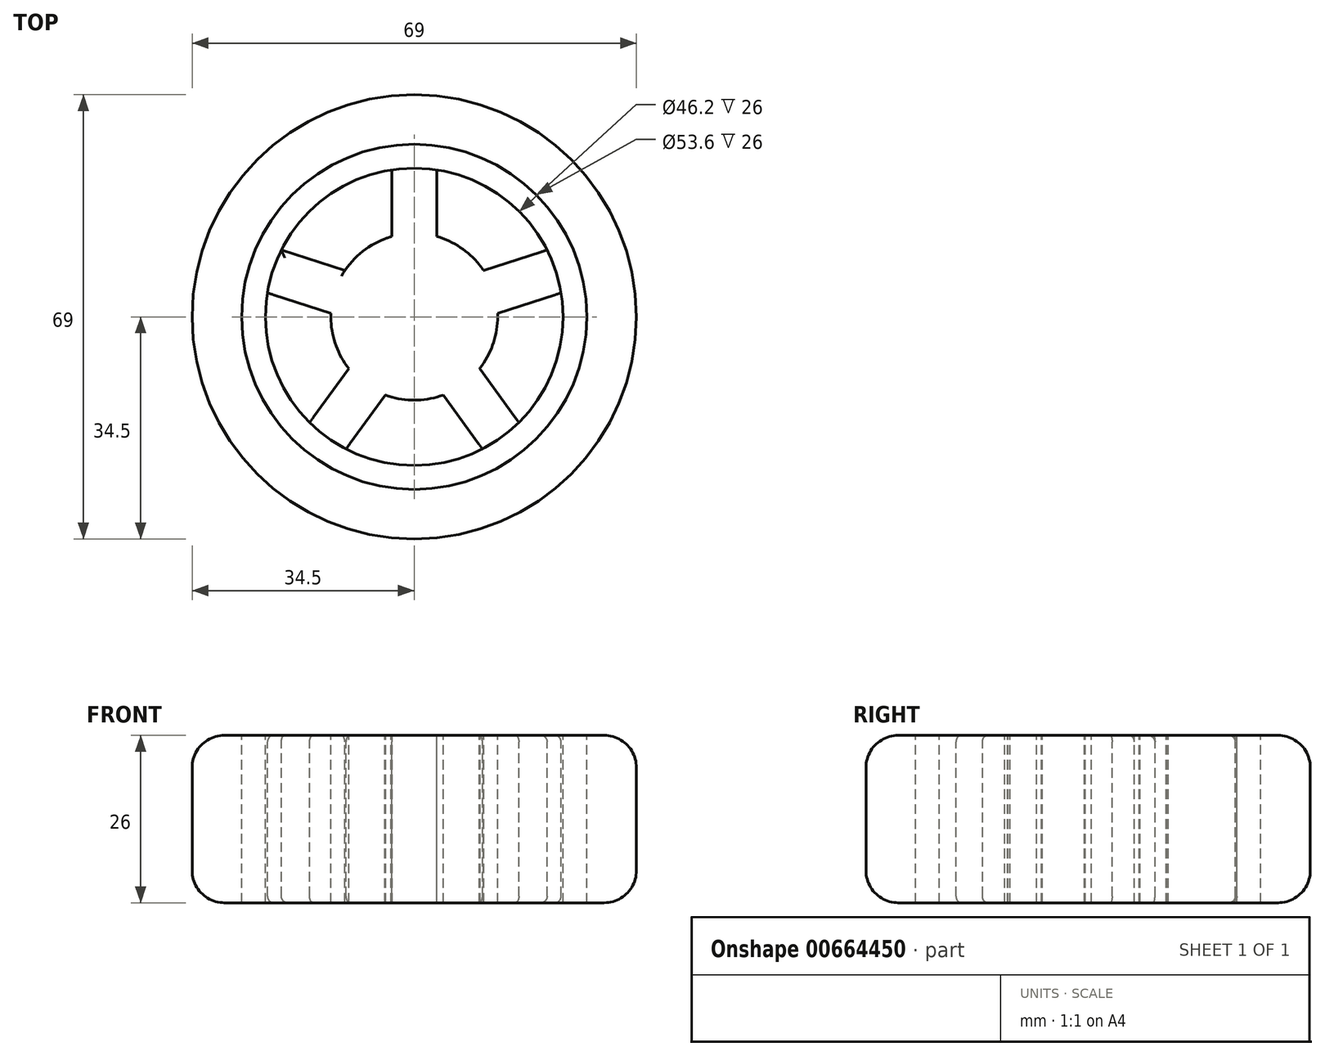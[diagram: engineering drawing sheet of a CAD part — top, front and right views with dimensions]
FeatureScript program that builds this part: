
annotation { "Feature Type Name" : "Feature", "Feature Type Description" : "" }
export const myFeature = defineFeature(function(context is Context, id is Id, definition is map)
    precondition{}
    {
        {
            var Q0;
            Q0=qCreatedBy(makeId("Top.planeOp"),FACE);
            var sketch = newSketch(context, id + "F0", { "sketchPlane" : qUnion([Q0])});
            skCircle(sketch, "E0", {"center": v(0, 0) * mm, "radius": 34.5 * mm});
            skCircle(sketch, "E1", {"center": v(0, 0) * mm, "radius": 26.8 * mm});
            skSolve(sketch);
        }
        {
            var Q0;
            Q0=makeQuery(id+"F0.imprint","IMPRINT",FACE,{"disambiguationData":[TD([[makeQuery(id+"F0.imprint","IMPRINT",EDGE,{"derivedFrom":sQuery(id+"F0.wireOp",EDGE,"E0")}),1.0]])]});
            extrude(context, id + "F1", {"entities" : qUnion([Q0]), "endBound" : BoundingType.SYMMETRIC, "depth" : 26 * mm, "offsetDistance" : 25 * mm});
        }
        {
            var Q0;
            Q0=makeQuery(id+"F1.opExtrude","CAP_FACE",FACE,{"disambiguationData":[OSD([sQuery(id+"F0.wireOp",EDGE,"E0"),sQuery(id+"F0.wireOp",EDGE,"E1")])],"isStart":false});
            var sketch = newSketch(context, id + "F2", { "sketchPlane" : qUnion([Q0])});
            skCircle(sketch, "E2", {"center": v(0, 0) * mm, "radius": 26.8 * mm});
            skCircle(sketch, "E3", {"center": v(0, 0) * mm, "radius": 23.1 * mm});
            skCircle(sketch, "E4", {"center": v(0, 0) * mm, "radius": 12.95 * mm});
            skLineSegment(sketch, "E5", {"start": v(-3.5, 12.47) * mm, "end": v(-3.5, 22.83) * mm});
            skLineSegment(sketch, "E6", {"start": v(3.5, 22.83) * mm, "end": v(3.5, 12.47) * mm});
            skArc(sketch, "E7", {"start": v(-4.56, 12.12) * mm, "mid": v(-3.8, 12.66) * mm, "end": v(-3.5, 13.55) * mm});
            skArc(sketch, "E8", {"start": v(3.5, 13.55) * mm, "mid": v(3.76, 12.72) * mm, "end": v(4.43, 12.17) * mm});
            skArc(sketch, "E9.1.0", {"start": v(-11.8, 7.52) * mm, "mid": v(-10.94, 7.5) * mm, "end": v(-10.2, 7.98) * mm});
            skLineSegment(sketch, "E9.1.1", {"start": v(-20.63, 10.38) * mm, "end": v(-10.78, 7.18) * mm});
            skLineSegment(sketch, "E9.1.2", {"start": v(-12.94, 0.52) * mm, "end": v(-22.8, 3.73) * mm});
            skArc(sketch, "E9.1.3", {"start": v(-12.94, -0.59) * mm, "mid": v(-13.22, 0.3) * mm, "end": v(-13.97, 0.86) * mm});
            skArc(sketch, "E9.2.0", {"start": v(-10.8, -8.9) * mm, "mid": v(-10.51, -8.08) * mm, "end": v(-10.74, -7.24) * mm});
            skLineSegment(sketch, "E9.2.1", {"start": v(-16.25, -16.42) * mm, "end": v(-10.16, -8.03) * mm});
            skLineSegment(sketch, "E9.2.2", {"start": v(-4.5, -12.14) * mm, "end": v(-10.59, -20.53) * mm});
            skArc(sketch, "E9.2.3", {"start": v(-3.44, -12.48) * mm, "mid": v(-4.38, -12.48) * mm, "end": v(-5.14, -13.02) * mm});
            skArc(sketch, "E9.3.0", {"start": v(5.14, -13.02) * mm, "mid": v(4.44, -12.5) * mm, "end": v(3.57, -12.45) * mm});
            skLineSegment(sketch, "E9.3.1", {"start": v(10.59, -20.53) * mm, "end": v(4.5, -12.14) * mm});
            skLineSegment(sketch, "E9.3.2", {"start": v(10.16, -8.03) * mm, "end": v(16.25, -16.42) * mm});
            skArc(sketch, "E9.3.3", {"start": v(10.81, -7.13) * mm, "mid": v(10.51, -8.02) * mm, "end": v(10.8, -8.9) * mm});
            skArc(sketch, "E9.4.0", {"start": v(13.97, 0.86) * mm, "mid": v(13.26, 0.36) * mm, "end": v(12.94, -0.46) * mm});
            skLineSegment(sketch, "E9.4.1", {"start": v(22.8, 3.73) * mm, "end": v(12.94, 0.52) * mm});
            skLineSegment(sketch, "E9.4.2", {"start": v(10.78, 7.18) * mm, "end": v(20.63, 10.38) * mm});
            skArc(sketch, "E9.4.3", {"start": v(10.12, 8.08) * mm, "mid": v(10.87, 7.52) * mm, "end": v(11.8, 7.52) * mm});
            skSolve(sketch);
        }
        {
            var Q0;
            {var subQ0=sQuery(id+"F2.wireOp",EDGE,"E5");var subQ1=sQuery(id+"F2.wireOp",EDGE,"E3");var subQ2=makeQuery(id+"F2.imprint","INTERSECT",VERTEX,{"derivedFrom":[subQ1,subQ0]});Q0=makeQuery(id+"F2.imprint","IMPRINT",FACE,{"disambiguationData":[TD([[makeQuery(id+"F2.imprint","IMPRINT",EDGE,{"disambiguationData":[TD([[subQ2,1.0]])],"derivedFrom":subQ1}),1.0]])]});}
            var Q1;
            {var subQ0=sQuery(id+"F2.wireOp",EDGE,"E4");var subQ21=makeQuery(id+"F2.imprint","INTERSECT",VERTEX,{"derivedFrom":[subQ0,sQuery(id+"F2.wireOp",EDGE,"E9.4.1")]});Q1=makeQuery(id+"F2.imprint","IMPRINT",FACE,{"disambiguationData":[TD([[makeQuery(id+"F2.imprint","IMPRINT",EDGE,{"disambiguationData":[TD([[subQ21,-1.0]])],"derivedFrom":subQ0}),1.0]])]});}
            var Q2;
            {var subQ0=sQuery(id+"F2.wireOp",EDGE,"E9.1.1");var subQ2=sQuery(id+"F2.wireOp",EDGE,"E3");var subQ3=makeQuery(id+"F2.imprint","INTERSECT",VERTEX,{"derivedFrom":[subQ2,subQ0]});Q2=makeQuery(id+"F2.imprint","IMPRINT",FACE,{"disambiguationData":[TD([[makeQuery(id+"F2.imprint","IMPRINT",EDGE,{"disambiguationData":[TD([[subQ3,-1.0]])],"derivedFrom":subQ2}),1.0]])]});}
            var Q3;
            {var subQ0=sQuery(id+"F2.wireOp",EDGE,"E9.2.1");var subQ2=sQuery(id+"F2.wireOp",EDGE,"E3");var subQ3=makeQuery(id+"F2.imprint","INTERSECT",VERTEX,{"derivedFrom":[subQ2,subQ0]});Q3=makeQuery(id+"F2.imprint","IMPRINT",FACE,{"disambiguationData":[TD([[makeQuery(id+"F2.imprint","IMPRINT",EDGE,{"disambiguationData":[TD([[subQ3,-1.0]])],"derivedFrom":subQ2}),1.0]])]});}
            var Q4;
            {var subQ0=sQuery(id+"F2.wireOp",EDGE,"E9.3.1");var subQ2=sQuery(id+"F2.wireOp",EDGE,"E3");var subQ3=makeQuery(id+"F2.imprint","INTERSECT",VERTEX,{"derivedFrom":[subQ2,subQ0]});Q4=makeQuery(id+"F2.imprint","IMPRINT",FACE,{"disambiguationData":[TD([[makeQuery(id+"F2.imprint","IMPRINT",EDGE,{"disambiguationData":[TD([[subQ3,-1.0]])],"derivedFrom":subQ2}),1.0]])]});}
            var Q5;
            {var subQ0=sQuery(id+"F2.wireOp",EDGE,"E9.4.1");var subQ2=sQuery(id+"F2.wireOp",EDGE,"E3");var subQ3=makeQuery(id+"F2.imprint","INTERSECT",VERTEX,{"derivedFrom":[subQ2,subQ0]});Q5=makeQuery(id+"F2.imprint","IMPRINT",FACE,{"disambiguationData":[TD([[makeQuery(id+"F2.imprint","IMPRINT",EDGE,{"disambiguationData":[TD([[subQ3,-1.0]])],"derivedFrom":subQ2}),1.0]])]});}
            extrude(context, id + "F3", {"entities" : qUnion([Q0, Q1, Q2, Q3, Q4, Q5]), "oppositeDirection" : true, "depth" : 26 * mm, "offsetDistance" : 25 * mm});
        }
        {
            var Q0;
            Q0=makeQuery(id+"F2.imprint","IMPRINT",FACE,{"disambiguationData":[TD([[makeQuery(id+"F2.imprint","IMPRINT",EDGE,{"derivedFrom":sQuery(id+"F2.wireOp",EDGE,"E2")}),1.0]])]});
            extrude(context, id + "F4", {"entities" : qUnion([Q0]), "oppositeDirection" : true, "depth" : 26 * mm, "offsetDistance" : 25 * mm});
        }
        {
            var Q0;
            Q0=makeQuery(id+"F1.opExtrude","CAP_EDGE",EDGE,{"disambiguationData":[OSD([sQuery(id+"F0.wireOp",EDGE,"E0")])],"isStart":true});
            var Q1;
            Q1=makeQuery(id+"F1.opExtrude","CAP_EDGE",EDGE,{"disambiguationData":[OSD([sQuery(id+"F0.wireOp",EDGE,"E0")])],"isStart":false});
            fillet(context, id + "F5", {"entities" : qUnion([Q0, Q1]), "radius" : 5 * mm, "tangentPropagation" : true, "allowEdgeOverflow" : false});
        }
        {
            var Q0;
            {var subQ0=sQuery(id+"F2.wireOp",EDGE,"E3");Q0=makeQuery(id+"F3.opExtrude","CAP_EDGE",EDGE,{"disambiguationData":[OSD([subQ0]),TDD([makeQuery(id+"F2.imprint","IMPRINT",EDGE,{"disambiguationData":[TD([[makeQuery(id+"F2.imprint","INTERSECT",VERTEX,{"derivedFrom":[subQ0,sQuery(id+"F2.wireOp",EDGE,"E9.2.1")]}),-1.0]])],"derivedFrom":subQ0})])],"isStart":false});}
            var Q1;
            {var subQ0=sQuery(id+"F2.wireOp",EDGE,"E3");Q1=makeQuery(id+"F3.opExtrude","CAP_EDGE",EDGE,{"disambiguationData":[OSD([subQ0]),TDD([makeQuery(id+"F2.imprint","IMPRINT",EDGE,{"disambiguationData":[TD([[makeQuery(id+"F2.imprint","INTERSECT",VERTEX,{"derivedFrom":[subQ0,sQuery(id+"F2.wireOp",EDGE,"E9.3.1")]}),-1.0]])],"derivedFrom":subQ0})])],"isStart":false});}
            var Q2;
            {var subQ0=sQuery(id+"F2.wireOp",EDGE,"E3");Q2=makeQuery(id+"F3.opExtrude","CAP_EDGE",EDGE,{"disambiguationData":[OSD([subQ0]),TDD([makeQuery(id+"F2.imprint","IMPRINT",EDGE,{"disambiguationData":[TD([[makeQuery(id+"F2.imprint","INTERSECT",VERTEX,{"derivedFrom":[subQ0,sQuery(id+"F2.wireOp",EDGE,"E9.4.1")]}),-1.0]])],"derivedFrom":subQ0})])],"isStart":false});}
            var Q3;
            {var subQ0=sQuery(id+"F2.wireOp",EDGE,"E3");Q3=makeQuery(id+"F3.opExtrude","CAP_EDGE",EDGE,{"disambiguationData":[OSD([subQ0]),TDD([makeQuery(id+"F2.imprint","IMPRINT",EDGE,{"disambiguationData":[TD([[makeQuery(id+"F2.imprint","INTERSECT",VERTEX,{"derivedFrom":[subQ0,sQuery(id+"F2.wireOp",EDGE,"E5")]}),1.0]])],"derivedFrom":subQ0})])],"isStart":false});}
            var Q4;
            {var subQ0=sQuery(id+"F2.wireOp",EDGE,"E3");Q4=makeQuery(id+"F3.opExtrude","CAP_EDGE",EDGE,{"disambiguationData":[OSD([subQ0]),TDD([makeQuery(id+"F2.imprint","IMPRINT",EDGE,{"disambiguationData":[TD([[makeQuery(id+"F2.imprint","INTERSECT",VERTEX,{"derivedFrom":[subQ0,sQuery(id+"F2.wireOp",EDGE,"E9.1.1")]}),-1.0]])],"derivedFrom":subQ0})])],"isStart":false});}
            var Q5;
            {var subQ0=sQuery(id+"F2.wireOp",EDGE,"E3");Q5=makeQuery(id+"F3.opExtrude","CAP_EDGE",EDGE,{"disambiguationData":[OSD([subQ0]),TDD([makeQuery(id+"F2.imprint","IMPRINT",EDGE,{"disambiguationData":[TD([[makeQuery(id+"F2.imprint","INTERSECT",VERTEX,{"derivedFrom":[subQ0,sQuery(id+"F2.wireOp",EDGE,"E9.1.1")]}),-1.0]])],"derivedFrom":subQ0})])],"isStart":true});}
            var Q6;
            {var subQ0=sQuery(id+"F2.wireOp",EDGE,"E3");Q6=makeQuery(id+"F3.opExtrude","CAP_EDGE",EDGE,{"disambiguationData":[OSD([subQ0]),TDD([makeQuery(id+"F2.imprint","IMPRINT",EDGE,{"disambiguationData":[TD([[makeQuery(id+"F2.imprint","INTERSECT",VERTEX,{"derivedFrom":[subQ0,sQuery(id+"F2.wireOp",EDGE,"E5")]}),1.0]])],"derivedFrom":subQ0})])],"isStart":true});}
            var Q7;
            {var subQ0=sQuery(id+"F2.wireOp",EDGE,"E3");Q7=makeQuery(id+"F3.opExtrude","CAP_EDGE",EDGE,{"disambiguationData":[OSD([subQ0]),TDD([makeQuery(id+"F2.imprint","IMPRINT",EDGE,{"disambiguationData":[TD([[makeQuery(id+"F2.imprint","INTERSECT",VERTEX,{"derivedFrom":[subQ0,sQuery(id+"F2.wireOp",EDGE,"E9.2.1")]}),-1.0]])],"derivedFrom":subQ0})])],"isStart":true});}
            var Q8;
            {var subQ0=sQuery(id+"F2.wireOp",EDGE,"E3");Q8=makeQuery(id+"F3.opExtrude","CAP_EDGE",EDGE,{"disambiguationData":[OSD([subQ0]),TDD([makeQuery(id+"F2.imprint","IMPRINT",EDGE,{"disambiguationData":[TD([[makeQuery(id+"F2.imprint","INTERSECT",VERTEX,{"derivedFrom":[subQ0,sQuery(id+"F2.wireOp",EDGE,"E9.3.1")]}),-1.0]])],"derivedFrom":subQ0})])],"isStart":true});}
            var Q9;
            {var subQ0=sQuery(id+"F2.wireOp",EDGE,"E3");Q9=makeQuery(id+"F3.opExtrude","CAP_EDGE",EDGE,{"disambiguationData":[OSD([subQ0]),TDD([makeQuery(id+"F2.imprint","IMPRINT",EDGE,{"disambiguationData":[TD([[makeQuery(id+"F2.imprint","INTERSECT",VERTEX,{"derivedFrom":[subQ0,sQuery(id+"F2.wireOp",EDGE,"E9.4.1")]}),-1.0]])],"derivedFrom":subQ0})])],"isStart":true});}
            var Q10;
            {var subQ0=sQuery(id+"F0.wireOp",EDGE,"E0");Q10=makeQuery(id+"F5.opFillet","BLEND_EDGE",EDGE,{"blendedFrom":[makeQuery(id+"F1.opExtrude","CAP_EDGE",EDGE,{"disambiguationData":[OSD([subQ0])],"isStart":true}),makeQuery(id+"F1.opExtrude","SWEPT_FACE",FACE,{"disambiguationData":[OSD([subQ0])]})],"blendedInto":[makeQuery(id+"F1.opExtrude","SWEPT_FACE",FACE,{"disambiguationData":[OSD([subQ0])]})]});}
            var Q11;
            Q11=makeQuery(id+"F3.opExtrude","CAP_EDGE",EDGE,{"disambiguationData":[OSD([sQuery(id+"F2.wireOp",EDGE,"E9.1.1")])],"isStart":true});
            fillet(context, id + "F6", {"entities" : qUnion([Q0, Q1, Q2, Q3, Q4, Q5, Q6, Q7, Q8, Q9, Q10, Q11]), "radius" : 1 * mm, "tangentPropagation" : true, "allowEdgeOverflow" : false});
        }
    });
